# Revit family: agtatec_Record_SldngDrset_THERMCORD-D-STA_CurtainWallPanel
name_source: partatom
category: Curtain Panels
revit_build: Autodesk Revit Architecture 2015 (Build: 20140606_1530(x64)
units: mm (PartAtom-declared; Revit-internal decimal feet)

## types (8) — shared parameters
AccessoryOptions = Contact manufacturer
AlternativeDoorsetGlazing = Part of glazing spec
AntiFingerTrapRequirement = Yes
Assembly Code = B2030110
BIMObjectName = agtatec_Record_SlidingDoorset_THERMCORD-D-STA_CurtainWallPanel
ClearHeightOfPassage = 2150 mm
ClearanceZones = No
Colour = Customer specific
Configuration = 1 or 2
Construction Type = Automatic Sliding Door
Description = Automatic Sliding Door
DoorIncluded = Yes
DoorSeal = 1
DoorsetFasteners = Screws
DoorsetOperation = Automatic
DriveUnit = agtatec_Record_Sliding Door, Sheet Metal (Painted Steel)
DurationUnit = year
ElectronicLock = Yes
Finish = Powder coated, Anodized, customer specific
FireExit = No
FloorGuide = agtatec_Record_Sliding Door, Stainless Steel
FrameMaterial = Aluminium
FrameProfile = Aluminium
FrameSeal = Yes
GlassLayers = 2
GlassThickness1 = 8 mm  [stored 0.0262467 ft]
GlassType = Part of glazing spec
HandicapAccessible = Yes
HasDrive = Yes
IfcExportAs = IfcDoorStyle
IfcExportType = Door
InnerPanelWidth = 646 mm  [stored 2.11942 ft]
InterlancingProfileHeight = 2195 mm
IsExternal = Yes
LeafColourOptions = All RAL, customer specific
ManufacturerName = Record
ManufacturerURL = www.agta-record.com
Material = Aluminium
Model = Thermcord D-STA
ModelReference = Depends on the configuration
NBSDescription = Sliding Doorset
NBSReference = 25-50-20/175
OpeningWidth = 1200 mm
OuterPanelWidthLeft = 613 mm
OuterPanelWidthRight = 613 mm
PanelFill = agtatec_Record_Sliding Door, Laminated Safety Glass (Clear)
PanelFrames = agtatec_Record_Sliding Door, Aluminium
PanelHeight = 2200 mm
ProductInformation = www.agta-record.com
ReferenceStandard = EN16005, EN16361, DIN 18650, etc.
ReplacementCost = Depends on the configuration and door type
SelfClosing = Yes
ServiceLifeDuration = 10-15 years
Shape = Rectangular
SidePanelMinimumStandard = 646 mm  [stored 2.11942 ft]
SidePanelWidthLeft = 646 mm  [stored 2.11942 ft]
SidePanelWidthRight = 646 mm  [stored 2.11942 ft]
SmokeStop = No
SupportLength = 2492 mm  [stored 8.17585 ft]
ThresholdRequired = Yes
ThresholdStripping = No additional required, part of the doorset
URL = www.agta-record.com
Uniclass2 = Ss_25_30_20_77
Version = Version 1.0
WallMountingProfile = No
WarrantyDescription = Depends on country
WarrantyDurationLabour = Depends on country
WarrantyDurationParts = Depends on country
WarrantyDurationUnit = Depends on country
WarrantyGuarantorLabour = Local door manufacturer
WarrantyGuarantorParts = Local door manufacturer
Weight = Depends on configuration and size
WithDriveCladding = Yes
WithinStandardSizes = Yes
WithoutDriveCladding(OnlyApplicableForTypesWithoutSidePanels) = No
zero-valued in all types: Cost, DoorOpening, DriveUnitExtraWidthLeft, DriveUnitExtraWidthRight, ExtraLeft, ExtraRight, ExtraWidthLeft, ExtraWidthRight, ExtraWidthTotal, GlassThickness2, NominalLength, ThermalTransmittance

## per-type parameters (varying)
| type | DriveUnitHeight | InterlancingProfile1 | LeftPanel | Name | NominalHeight | NominalWidth | RightPanel | TotalHeight | TotalWidth | WithSidePanels | WithoutSidePanels |
| THERMCORD D-STA 150mm drive unit height side panel left | 150 mm | No | Yes | SldngDrset_THERMCORD-D-STA_CurtainWallPanel_Record | 2300 mm | 1901 mm | No | 2300 mm | 1901 mm | No | No |
| THERMCORD D-STA 150mm drive unit height side panel right | 150 mm | No | No | SldngDrset_THERMCORD-D-STA_CurtainWallPanel_Record | 2300 mm | 1901 mm | Yes | 2300 mm | 1901 mm | No | No |
| THERMCORD D-STA 150mm drive unit height with two side panels | 150 mm | Yes | Yes | SldngDrset_THERMCORD-D-STA_CurtainWallpanel_Record | 2300 mm | 2492 mm  [stored 8.17585 ft] | Yes | 2300 mm | 2492 mm  [stored 8.17585 ft] | Yes | No |
| THERMCORD D-STA 150mm drive unit height without side panels | 150 mm | No | No | SldngDrset_THERMCORD-D-STA_CurtainWallPanel_Record | 2300 mm | 1309 mm | No | 2300 mm | 1309 mm | No | Yes |
| THERMCORD D-STA 200mm drive unit height side panel left | 200 mm  [stored 0.656168 ft] | No | Yes | SldngDrset_THERMCORD-D-STA_CurtainWallPanel_Record | 2350 mm | 1901 mm | No | 2350 mm | 1901 mm | No | No |
| THERMCORD D-STA 200mm drive unit height side panel right | 200 mm  [stored 0.656168 ft] | No | No | SldngDrset_THERMCORD-D-STA_CurtainWallPanel_Record | 2350 mm | 1901 mm | Yes | 2350 mm | 1901 mm | No | No |
| THERMCORD D-STA 200mm drive unit height with two side panels | 200 mm  [stored 0.656168 ft] | Yes | Yes | SldngDrset_THERMCORD-D-STA_CurtainWallPanel_Record | 2350 mm | 2492 mm  [stored 8.17585 ft] | Yes | 2350 mm | 2492 mm  [stored 8.17585 ft] | Yes | No |
| THERMCORD D-STA 200mm drive unit height without side panels | 200 mm  [stored 0.656168 ft] | No | No | SldngDrset_THERMCORD-D-STA_CurtainWallPanel_Record | 2350 mm | 1309 mm | No | 2350 mm | 1309 mm | No | Yes |

note: [stored X ft] marks values corroborated as IEEE doubles in the binary element streams (Revit-internal decimal feet)

## geometry (parser evidence)
native form markers: Blend x8, Sweep x16
no freeform markers — native parametric forms only
